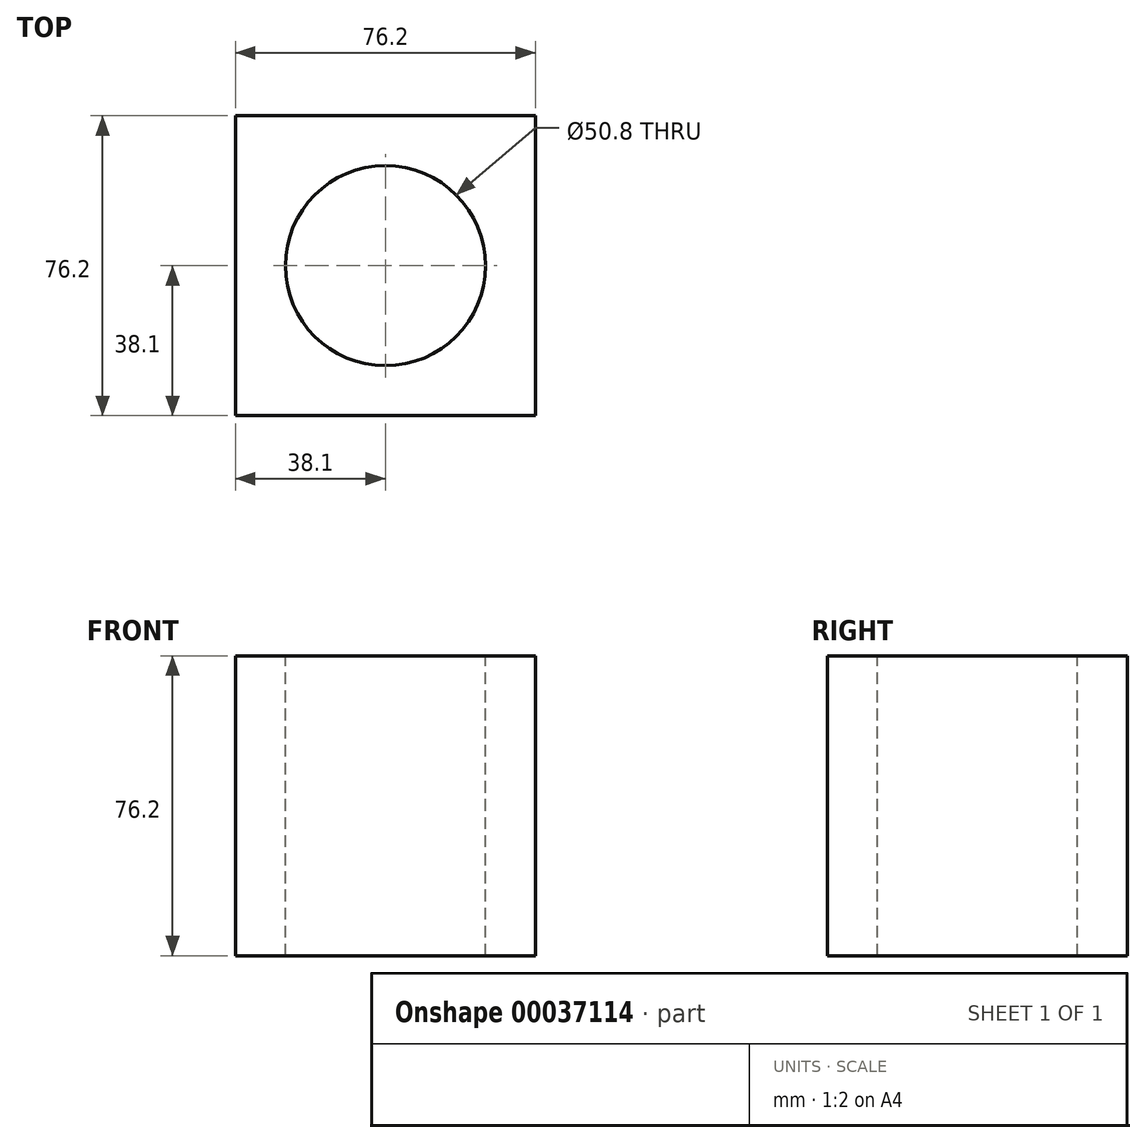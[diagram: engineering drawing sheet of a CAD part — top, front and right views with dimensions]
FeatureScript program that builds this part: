
annotation { "Feature Type Name" : "Feature", "Feature Type Description" : "" }
export const myFeature = defineFeature(function(context is Context, id is Id, definition is map)
    precondition{}
    {
        {
            var Q0;
            Q0=qCreatedBy(makeId("Top.planeOp"),FACE);
            var sketch = newSketch(context, id + "F0", { "sketchPlane" : qUnion([Q0])});
            skLineSegment(sketch, "E0.bottom", {"start": v(0, 0) * mm, "end": v(76.2, 0) * mm});
            skLineSegment(sketch, "E0.top", {"start": v(0, 76.2) * mm, "end": v(76.2, 76.2) * mm});
            skLineSegment(sketch, "E0.left", {"start": v(0, 0) * mm, "end": v(0, 76.2) * mm});
            skLineSegment(sketch, "E0.right", {"start": v(76.2, 0) * mm, "end": v(76.2, 76.2) * mm});
            skSolve(sketch);
        }
        {
            var Q0;
            Q0 = qSketchRegion(id + "F0", true);
            extrude(context, id + "F1", {"entities" : qUnion([Q0]), "depth" : 76.2 * mm});
        }
        {
            var Q0;
            Q0=makeQuery(id+"F1.opExtrude","CAP_FACE",FACE,{"disambiguationData":[OSD([sQuery(id+"F0.wireOp",EDGE,"E0.bottom"),sQuery(id+"F0.wireOp",EDGE,"E0.top"),sQuery(id+"F0.wireOp",EDGE,"E0.left"),sQuery(id+"F0.wireOp",EDGE,"E0.right")])],"isStart":false});
            var sketch = newSketch(context, id + "F2", { "sketchPlane" : qUnion([Q0])});
            skCircle(sketch, "E1", {"center": v(38.1, 38.1) * mm, "radius": 25.4 * mm});
            skSolve(sketch);
        }
        {
            var Q0;
            Q0 = qSketchRegion(id + "F2", true);
            var Q1;
            Q1=makeQuery(id+"F1.opExtrude","CAP_FACE",FACE,{"disambiguationData":[OSD([sQuery(id+"F0.wireOp",EDGE,"E0.bottom"),sQuery(id+"F0.wireOp",EDGE,"E0.top"),sQuery(id+"F0.wireOp",EDGE,"E0.left"),sQuery(id+"F0.wireOp",EDGE,"E0.right")])],"isStart":true});
            extrude(context, id + "F3", {"entities" : qUnion([Q0]), "operationType" : NewBodyOperationType.REMOVE, "endBound" : BoundingType.UP_TO_SURFACE, "oppositeDirection" : true, "endBoundEntityFace" : qUnion([Q1]), "depth" : 25.4 * mm});
        }
    });
